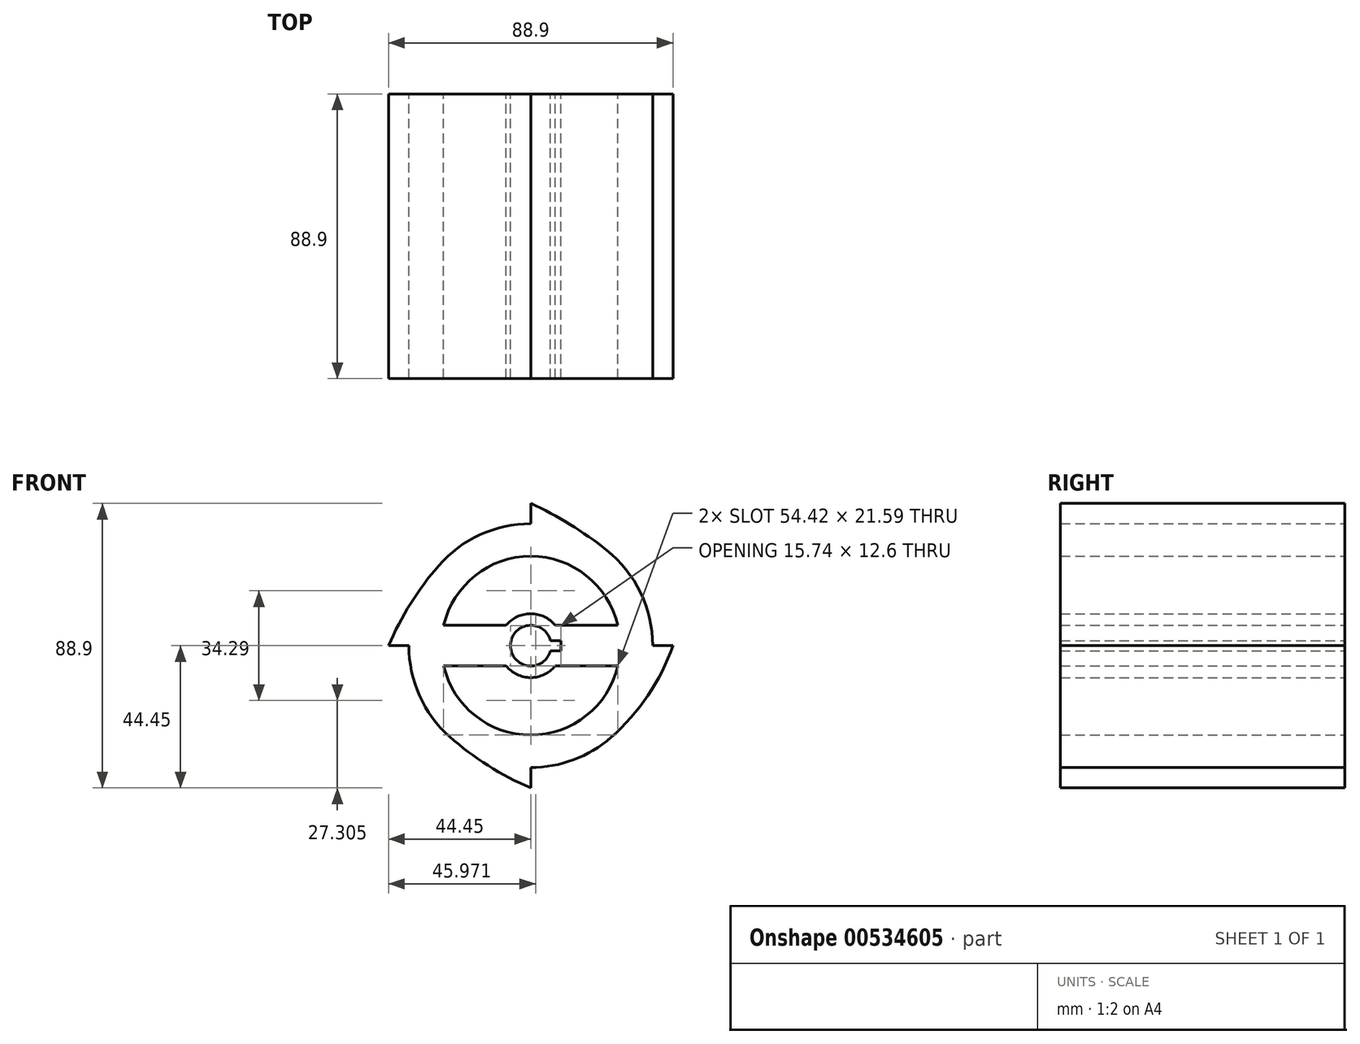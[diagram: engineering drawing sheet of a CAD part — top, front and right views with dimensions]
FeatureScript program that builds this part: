
annotation { "Feature Type Name" : "Feature", "Feature Type Description" : "" }
export const myFeature = defineFeature(function(context is Context, id is Id, definition is map)
    precondition{}
    {
        {
            var Q0;
            Q0=qCreatedBy(makeId("Front.planeOp"),FACE);
            var sketch = newSketch(context, id + "F0", { "sketchPlane" : qUnion([Q0])});
            skCircle(sketch, "E0", {"center": v(0, 0) * mm, "radius": 38.1 * mm});
            skLineSegment(sketch, "E1", {"start": v(-44.45, 0) * mm, "end": v(44.45, 0) * mm});
            skArc(sketch, "E2", {"start": v(23.7, 29.83) * mm, "mid": v(12.29, 37.84) * mm, "end": v(0, 44.45) * mm});
            skArc(sketch, "E3", {"start": v(-28.78, 24.96) * mm, "mid": v(-37.58, 13.09) * mm, "end": v(-44.45, 0) * mm});
            skArc(sketch, "E4", {"start": v(-25.36, -28.44) * mm, "mid": v(-13.34, -37.5) * mm, "end": v(0, -44.45) * mm});
            skArc(sketch, "E5", {"start": v(25.05, -28.7) * mm, "mid": v(36.62, -15.62) * mm, "end": v(44.45, 0) * mm});
            skArc(sketch, "E6", {"start": v(27.2, 6.35) * mm, "mid": v(0, 27.94) * mm, "end": v(-27.2, 6.35) * mm});
            skArc(sketch, "E7", {"start": v(-27.2, -6.35) * mm, "mid": v(0, -27.94) * mm, "end": v(27.2, -6.35) * mm});
            skCircle(sketch, "E8", {"center": v(0, 0) * mm, "radius": 6.35 * mm});
            skLineSegment(sketch, "E9.bottom", {"start": v(-9.4, 1.59) * mm, "end": v(9.4, 1.59) * mm});
            skLineSegment(sketch, "E9.top", {"start": v(-9.4, -1.59) * mm, "end": v(9.4, -1.59) * mm});
            skLineSegment(sketch, "E9.left", {"start": v(-9.4, 1.59) * mm, "end": v(-9.4, -1.59) * mm});
            skLineSegment(sketch, "E9.right", {"start": v(9.4, 1.59) * mm, "end": v(9.4, -1.59) * mm});
            skLineSegment(sketch, "E10", {"start": v(-27.2, -6.35) * mm, "end": v(-7.7, -6.35) * mm});
            skLineSegment(sketch, "E11", {"start": v(-27.2, 6.35) * mm, "end": v(-7.7, 6.35) * mm});
            skLineSegment(sketch, "E12", {"start": v(27.2, -6.35) * mm, "end": v(7.7, -6.35) * mm});
            skLineSegment(sketch, "E13", {"start": v(27.2, 6.35) * mm, "end": v(7.7, 6.35) * mm});
            skCircle(sketch, "E14", {"center": v(0, 0) * mm, "radius": 9.97 * mm});
            skLineSegment(sketch, "E15", {"start": v(0, -44.45) * mm, "end": v(0, -38.1) * mm});
            skLineSegment(sketch, "E16", {"start": v(0, 44.45) * mm, "end": v(0, 38.1) * mm});
            skSolve(sketch);
        }
        {
            var Q0;
            Q0=qSketchRegion(id+"F0",true);
            var Q1;
            {var subQ5=sQuery(id+"F0.wireOp",EDGE,"E14");var subQ6=sQuery(id+"F0.wireOp",EDGE,"E1");var subQ7=makeQuery(id+"F0.imprint","INTERSECT",VERTEX,{"disambiguationData":[OD(0.0)],"derivedFrom":[subQ6,subQ5]});Q1=makeQuery(id+"F0.imprint","IMPRINT",FACE,{"disambiguationData":[TD([[makeQuery(id+"F0.imprint","IMPRINT",EDGE,{"disambiguationData":[TD([[subQ7,-1.0]])],"derivedFrom":subQ6}),-1.0]])]});}
            var Q2;
            {var subQ6=sQuery(id+"F0.wireOp",EDGE,"E1");var subQ10=sQuery(id+"F0.wireOp",EDGE,"E14");var subQ12=makeQuery(id+"F0.imprint","INTERSECT",VERTEX,{"disambiguationData":[OD(0.0)],"derivedFrom":[subQ6,subQ10]});Q2=makeQuery(id+"F0.imprint","IMPRINT",FACE,{"disambiguationData":[TD([[makeQuery(id+"F0.imprint","IMPRINT",EDGE,{"disambiguationData":[TD([[subQ12,-1.0]])],"derivedFrom":subQ6}),1.0]])]});}
            var Q3;
            {var subQ0=sQuery(id+"F0.wireOp",EDGE,"E9.left");var subQ1=sQuery(id+"F0.wireOp",EDGE,"E1");var subQ2=makeQuery(id+"F0.imprint","INTERSECT",VERTEX,{"derivedFrom":[subQ1,subQ0]});Q3=makeQuery(id+"F0.imprint","IMPRINT",FACE,{"disambiguationData":[TD([[makeQuery(id+"F0.imprint","IMPRINT",EDGE,{"disambiguationData":[TD([[subQ2,-1.0]])],"derivedFrom":subQ1}),1.0]])]});}
            var Q4;
            {var subQ0=sQuery(id+"F0.wireOp",EDGE,"E9.left");var subQ1=sQuery(id+"F0.wireOp",EDGE,"E1");var subQ2=makeQuery(id+"F0.imprint","INTERSECT",VERTEX,{"derivedFrom":[subQ1,subQ0]});Q4=makeQuery(id+"F0.imprint","IMPRINT",FACE,{"disambiguationData":[TD([[makeQuery(id+"F0.imprint","IMPRINT",EDGE,{"disambiguationData":[TD([[subQ2,-1.0]])],"derivedFrom":subQ1}),-1.0]])]});}
            extrude(context, id + "F1", {"entities" : qUnion([Q0, Q1, Q2, Q3, Q4]), "depth" : 88.9 * mm, "offsetDistance" : 25.4 * mm});
        }
    });
